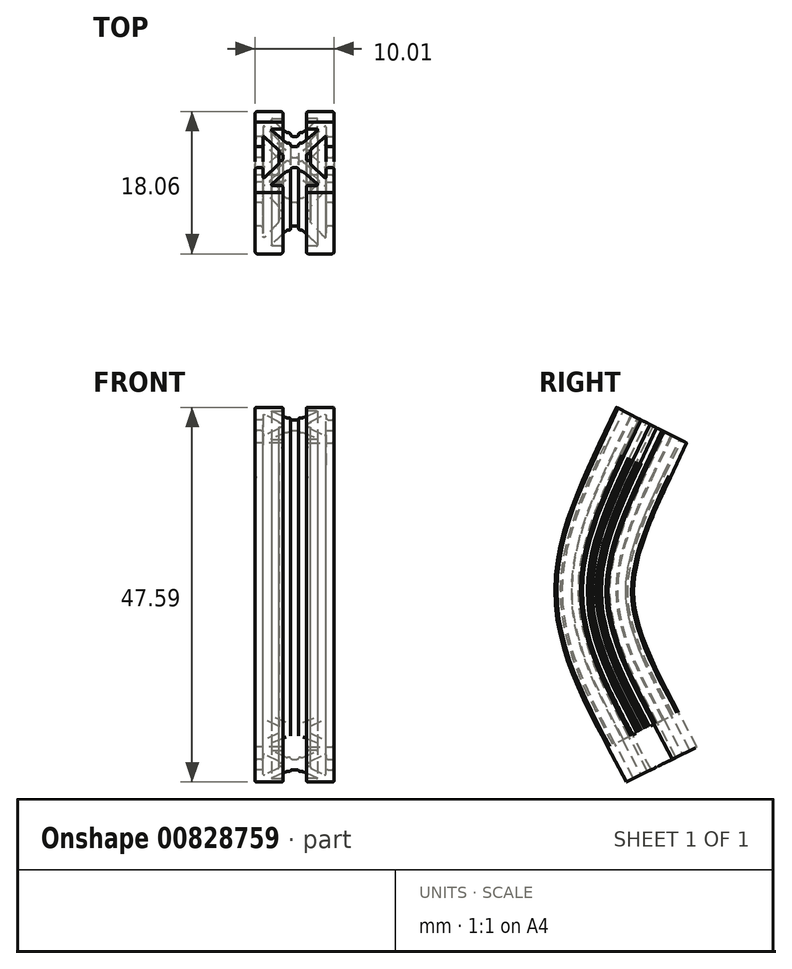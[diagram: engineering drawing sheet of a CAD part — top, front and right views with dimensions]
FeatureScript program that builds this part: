
annotation { "Feature Type Name" : "Feature", "Feature Type Description" : "" }
export const myFeature = defineFeature(function(context is Context, id is Id, definition is map)
    precondition{}
    {
        {
            var Q0;
            Q0=qCreatedBy(makeId("Top.planeOp"),FACE);
            var sketch = newSketch(context, id + "F0", { "sketchPlane" : qUnion([Q0])});
            skArc(sketch, "E0", {"start": v(2.9, 3.8) * mm, "mid": v(2.92, 3.93) * mm, "end": v(2.8, 4.01) * mm});
            skArc(sketch, "E1", {"start": v(0.75, 2) * mm, "mid": v(0.57, 1.93) * mm, "end": v(0.5, 1.75) * mm});
            skArc(sketch, "E2", {"start": v(0.89, 2) * mm, "mid": v(0.98, 2.02) * mm, "end": v(1.06, 2.08) * mm});
            skArc(sketch, "E3", {"start": v(1.5, 4.27) * mm, "mid": v(1.57, 4.09) * mm, "end": v(1.75, 4.01) * mm});
            skArc(sketch, "E4", {"start": v(1.75, 5) * mm, "mid": v(1.57, 4.93) * mm, "end": v(1.5, 4.75) * mm});
            skArc(sketch, "E5", {"start": v(0.24, 1.5) * mm, "mid": v(0.42, 1.57) * mm, "end": v(0.5, 1.75) * mm});
            skArc(sketch, "E6", {"start": v(4.75, 1.5) * mm, "mid": v(4.93, 1.57) * mm, "end": v(5, 1.75) * mm});
            skArc(sketch, "E7", {"start": v(4.01, 1.75) * mm, "mid": v(4.09, 1.57) * mm, "end": v(4.27, 1.5) * mm});
            skArc(sketch, "E8", {"start": v(4.01, 2.8) * mm, "mid": v(3.93, 2.92) * mm, "end": v(3.8, 2.9) * mm});
            skArc(sketch, "E9", {"start": v(2.08, 1.06) * mm, "mid": v(2.02, 0.98) * mm, "end": v(2, 0.89) * mm});
            skArc(sketch, "E10", {"start": v(1.75, 0.5) * mm, "mid": v(1.93, 0.57) * mm, "end": v(2, 0.75) * mm});
            skArc(sketch, "E11", {"start": v(1.75, 0.5) * mm, "mid": v(1.57, 0.42) * mm, "end": v(1.5, 0.24) * mm});
            skArc(sketch, "E12", {"start": v(0.5, -1.75) * mm, "mid": v(0.42, -1.57) * mm, "end": v(0.24, -1.5) * mm});
            skArc(sketch, "E13", {"start": v(0.5, -1.75) * mm, "mid": v(0.57, -1.93) * mm, "end": v(0.75, -2) * mm});
            skArc(sketch, "E14", {"start": v(1.06, -2.08) * mm, "mid": v(0.98, -2.02) * mm, "end": v(0.89, -2) * mm});
            skArc(sketch, "E15", {"start": v(2.8, -4.01) * mm, "mid": v(2.92, -3.93) * mm, "end": v(2.9, -3.8) * mm});
            skArc(sketch, "E16", {"start": v(1.75, -4.01) * mm, "mid": v(1.57, -4.09) * mm, "end": v(1.5, -4.27) * mm});
            skArc(sketch, "E17", {"start": v(1.5, -4.75) * mm, "mid": v(1.57, -4.93) * mm, "end": v(1.75, -5) * mm});
            skArc(sketch, "E18", {"start": v(5, -1.75) * mm, "mid": v(4.93, -1.57) * mm, "end": v(4.75, -1.5) * mm});
            skArc(sketch, "E19", {"start": v(4.27, -1.5) * mm, "mid": v(4.09, -1.57) * mm, "end": v(4.01, -1.75) * mm});
            skArc(sketch, "E20", {"start": v(3.8, -2.9) * mm, "mid": v(3.93, -2.92) * mm, "end": v(4.01, -2.8) * mm});
            skArc(sketch, "E21", {"start": v(2, -0.89) * mm, "mid": v(2.02, -0.98) * mm, "end": v(2.08, -1.06) * mm});
            skArc(sketch, "E22", {"start": v(2, -0.75) * mm, "mid": v(1.93, -0.57) * mm, "end": v(1.75, -0.5) * mm});
            skArc(sketch, "E23", {"start": v(1.5, -0.24) * mm, "mid": v(1.57, -0.42) * mm, "end": v(1.75, -0.5) * mm});
            skArc(sketch, "E24", {"start": v(-0.5, 1.75) * mm, "mid": v(-0.42, 1.57) * mm, "end": v(-0.24, 1.5) * mm});
            skArc(sketch, "E25", {"start": v(-0.5, 1.75) * mm, "mid": v(-0.57, 1.93) * mm, "end": v(-0.75, 2) * mm});
            skArc(sketch, "E26", {"start": v(-1.06, 2.08) * mm, "mid": v(-0.98, 2.02) * mm, "end": v(-0.89, 2) * mm});
            skArc(sketch, "E27", {"start": v(-2.8, 4.01) * mm, "mid": v(-2.92, 3.93) * mm, "end": v(-2.9, 3.8) * mm});
            skArc(sketch, "E28", {"start": v(-1.75, 4.01) * mm, "mid": v(-1.57, 4.09) * mm, "end": v(-1.5, 4.27) * mm});
            skArc(sketch, "E29", {"start": v(-1.5, 4.75) * mm, "mid": v(-1.57, 4.93) * mm, "end": v(-1.75, 5) * mm});
            skArc(sketch, "E30", {"start": v(-5, 1.75) * mm, "mid": v(-4.93, 1.57) * mm, "end": v(-4.75, 1.5) * mm});
            skArc(sketch, "E31", {"start": v(-4.27, 1.5) * mm, "mid": v(-4.09, 1.57) * mm, "end": v(-4.01, 1.75) * mm});
            skArc(sketch, "E32", {"start": v(-3.8, 2.9) * mm, "mid": v(-3.93, 2.92) * mm, "end": v(-4.01, 2.8) * mm});
            skArc(sketch, "E33", {"start": v(-2, 0.89) * mm, "mid": v(-2.02, 0.98) * mm, "end": v(-2.08, 1.06) * mm});
            skArc(sketch, "E34", {"start": v(-2, 0.75) * mm, "mid": v(-1.93, 0.57) * mm, "end": v(-1.75, 0.5) * mm});
            skArc(sketch, "E35", {"start": v(-1.5, 0.24) * mm, "mid": v(-1.57, 0.42) * mm, "end": v(-1.75, 0.5) * mm});
            skArc(sketch, "E36", {"start": v(-1.75, -0.5) * mm, "mid": v(-1.57, -0.42) * mm, "end": v(-1.5, -0.24) * mm});
            skArc(sketch, "E37", {"start": v(-1.75, -0.5) * mm, "mid": v(-1.93, -0.57) * mm, "end": v(-2, -0.75) * mm});
            skArc(sketch, "E38", {"start": v(-2.08, -1.06) * mm, "mid": v(-2.02, -0.98) * mm, "end": v(-2, -0.89) * mm});
            skArc(sketch, "E39", {"start": v(-4.01, -2.8) * mm, "mid": v(-3.93, -2.92) * mm, "end": v(-3.8, -2.9) * mm});
            skArc(sketch, "E40", {"start": v(-4.01, -1.75) * mm, "mid": v(-4.09, -1.57) * mm, "end": v(-4.27, -1.5) * mm});
            skArc(sketch, "E41", {"start": v(-4.75, -1.5) * mm, "mid": v(-4.93, -1.57) * mm, "end": v(-5, -1.75) * mm});
            skArc(sketch, "E42", {"start": v(-1.75, -5) * mm, "mid": v(-1.57, -4.93) * mm, "end": v(-1.5, -4.75) * mm});
            skArc(sketch, "E43", {"start": v(-1.5, -4.27) * mm, "mid": v(-1.57, -4.09) * mm, "end": v(-1.75, -4.01) * mm});
            skArc(sketch, "E44", {"start": v(-2.9, -3.8) * mm, "mid": v(-2.92, -3.93) * mm, "end": v(-2.8, -4.01) * mm});
            skArc(sketch, "E45", {"start": v(-0.89, -2) * mm, "mid": v(-0.98, -2.02) * mm, "end": v(-1.06, -2.08) * mm});
            skArc(sketch, "E46", {"start": v(-0.75, -2) * mm, "mid": v(-0.57, -1.93) * mm, "end": v(-0.5, -1.75) * mm});
            skArc(sketch, "E47", {"start": v(-0.24, -1.5) * mm, "mid": v(-0.42, -1.57) * mm, "end": v(-0.5, -1.75) * mm});
            skArc(sketch, "E48", {"start": v(-4.75, 5) * mm, "mid": v(-4.93, 4.93) * mm, "end": v(-5, 4.75) * mm});
            skArc(sketch, "E49", {"start": v(-5, -4.75) * mm, "mid": v(-4.93, -4.93) * mm, "end": v(-4.75, -5) * mm});
            skArc(sketch, "E50", {"start": v(4.75, -5) * mm, "mid": v(4.93, -4.93) * mm, "end": v(5, -4.75) * mm});
            skArc(sketch, "E51", {"start": v(5, 4.75) * mm, "mid": v(4.93, 4.93) * mm, "end": v(4.75, 5) * mm});
            skLineSegment(sketch, "E52", {"start": v(-0.24, 1.5) * mm, "end": v(0.24, 1.5) * mm});
            skLineSegment(sketch, "E53", {"start": v(5, 1.75) * mm, "end": v(5, 4.75) * mm});
            skLineSegment(sketch, "E54", {"start": v(0.75, 2) * mm, "end": v(0.89, 2) * mm});
            skLineSegment(sketch, "E55", {"start": v(1.06, 2.08) * mm, "end": v(2.9, 3.8) * mm});
            skLineSegment(sketch, "E56", {"start": v(2.8, 4.01) * mm, "end": v(1.75, 4.01) * mm});
            skLineSegment(sketch, "E57", {"start": v(1.5, 4.27) * mm, "end": v(1.5, 4.75) * mm});
            skLineSegment(sketch, "E58", {"start": v(1.75, 5) * mm, "end": v(4.75, 5) * mm});
            skLineSegment(sketch, "E59", {"start": v(4.27, 1.5) * mm, "end": v(4.75, 1.5) * mm});
            skLineSegment(sketch, "E60", {"start": v(4.01, 2.8) * mm, "end": v(4.01, 1.75) * mm});
            skLineSegment(sketch, "E61", {"start": v(2.08, 1.06) * mm, "end": v(3.8, 2.9) * mm});
            skLineSegment(sketch, "E62", {"start": v(2, 0.75) * mm, "end": v(2, 0.89) * mm});
            skLineSegment(sketch, "E63", {"start": v(1.5, -0.24) * mm, "end": v(1.5, 0.24) * mm});
            skLineSegment(sketch, "E64", {"start": v(-0.24, -1.5) * mm, "end": v(0.24, -1.5) * mm});
            skLineSegment(sketch, "E65", {"start": v(0.75, -2) * mm, "end": v(0.89, -2) * mm});
            skLineSegment(sketch, "E66", {"start": v(1.06, -2.08) * mm, "end": v(2.9, -3.8) * mm});
            skLineSegment(sketch, "E67", {"start": v(2.8, -4.01) * mm, "end": v(1.75, -4.01) * mm});
            skLineSegment(sketch, "E68", {"start": v(1.5, -4.27) * mm, "end": v(1.5, -4.75) * mm});
            skLineSegment(sketch, "E69", {"start": v(1.75, -5) * mm, "end": v(4.75, -5) * mm});
            skLineSegment(sketch, "E70", {"start": v(5, -1.75) * mm, "end": v(5, -4.75) * mm});
            skLineSegment(sketch, "E71", {"start": v(4.27, -1.5) * mm, "end": v(4.75, -1.5) * mm});
            skLineSegment(sketch, "E72", {"start": v(4.01, -2.8) * mm, "end": v(4.01, -1.75) * mm});
            skLineSegment(sketch, "E73", {"start": v(2.08, -1.06) * mm, "end": v(3.8, -2.9) * mm});
            skLineSegment(sketch, "E74", {"start": v(2, -0.75) * mm, "end": v(2, -0.89) * mm});
            skLineSegment(sketch, "E75", {"start": v(-0.75, 2) * mm, "end": v(-0.89, 2) * mm});
            skLineSegment(sketch, "E76", {"start": v(-1.06, 2.08) * mm, "end": v(-2.9, 3.8) * mm});
            skLineSegment(sketch, "E77", {"start": v(-2.8, 4.01) * mm, "end": v(-1.75, 4.01) * mm});
            skLineSegment(sketch, "E78", {"start": v(-1.5, 4.27) * mm, "end": v(-1.5, 4.75) * mm});
            skLineSegment(sketch, "E79", {"start": v(-1.75, 5) * mm, "end": v(-4.75, 5) * mm});
            skLineSegment(sketch, "E80", {"start": v(-5, 1.75) * mm, "end": v(-5, 4.75) * mm});
            skLineSegment(sketch, "E81", {"start": v(-4.27, 1.5) * mm, "end": v(-4.75, 1.5) * mm});
            skLineSegment(sketch, "E82", {"start": v(-4.01, 2.8) * mm, "end": v(-4.01, 1.75) * mm});
            skLineSegment(sketch, "E83", {"start": v(-2.08, 1.06) * mm, "end": v(-3.8, 2.9) * mm});
            skLineSegment(sketch, "E84", {"start": v(-2, 0.75) * mm, "end": v(-2, 0.89) * mm});
            skLineSegment(sketch, "E85", {"start": v(-1.5, -0.24) * mm, "end": v(-1.5, 0.24) * mm});
            skLineSegment(sketch, "E86", {"start": v(-2, -0.75) * mm, "end": v(-2, -0.89) * mm});
            skLineSegment(sketch, "E87", {"start": v(-2.08, -1.06) * mm, "end": v(-3.8, -2.9) * mm});
            skLineSegment(sketch, "E88", {"start": v(-4.01, -2.8) * mm, "end": v(-4.01, -1.75) * mm});
            skLineSegment(sketch, "E89", {"start": v(-4.27, -1.5) * mm, "end": v(-4.75, -1.5) * mm});
            skLineSegment(sketch, "E90", {"start": v(-5, -1.75) * mm, "end": v(-5, -4.75) * mm});
            skLineSegment(sketch, "E91", {"start": v(-1.75, -5) * mm, "end": v(-4.75, -5) * mm});
            skLineSegment(sketch, "E92", {"start": v(-1.5, -4.27) * mm, "end": v(-1.5, -4.75) * mm});
            skLineSegment(sketch, "E93", {"start": v(-2.8, -4.01) * mm, "end": v(-1.75, -4.01) * mm});
            skLineSegment(sketch, "E94", {"start": v(-1.06, -2.08) * mm, "end": v(-2.9, -3.8) * mm});
            skLineSegment(sketch, "E95", {"start": v(-0.75, -2) * mm, "end": v(-0.89, -2) * mm});
            skSolve(sketch);
        }
        {
            var Q0;
            Q0=qCreatedBy(makeId("Right.planeOp"),FACE);
            var sketch = newSketch(context, id + "F1", { "sketchPlane" : qUnion([Q0])});
            skFitSpline(sketch, "E96", {"points": [v(6.22, -17.12) * mm, v(0, 0) * mm, v(5.12, 17.05) * mm], "startDerivative": vector(-18.08, 33.97) * mm, "endDerivative": vector(15.94, 34.37) * mm});
            skLineSegment(sketch, "E97", {"start": v(6.22, -17.12) * mm, "end": v(8.57, -21.53) * mm});
            skLineSegment(sketch, "E98", {"start": v(5.12, 17.05) * mm, "end": v(7.26, 21.57) * mm});
            skSolve(sketch);
        }
        {
            var Q0;
            Q0=makeQuery(id+"F0.imprint","IMPRINT",FACE,{"disambiguationData":[TD([[makeQuery(id+"F0.imprint","IMPRINT",EDGE,{"derivedFrom":sQuery(id+"F0.wireOp",EDGE,"E0")}),-1.0]])]});
            var Q1;
            Q1=sQuery(id+"F1.wireOp",EDGE,"E97");
            var Q2;
            Q2=sQuery(id+"F1.wireOp",EDGE,"E96");
            var Q3;
            Q3=sQuery(id+"F1.wireOp",EDGE,"E98");
            sweep(context, id + "F2", {"profiles" : qUnion([Q0]), "path" : qUnion([Q1, Q2, Q3])});
        }
    });
